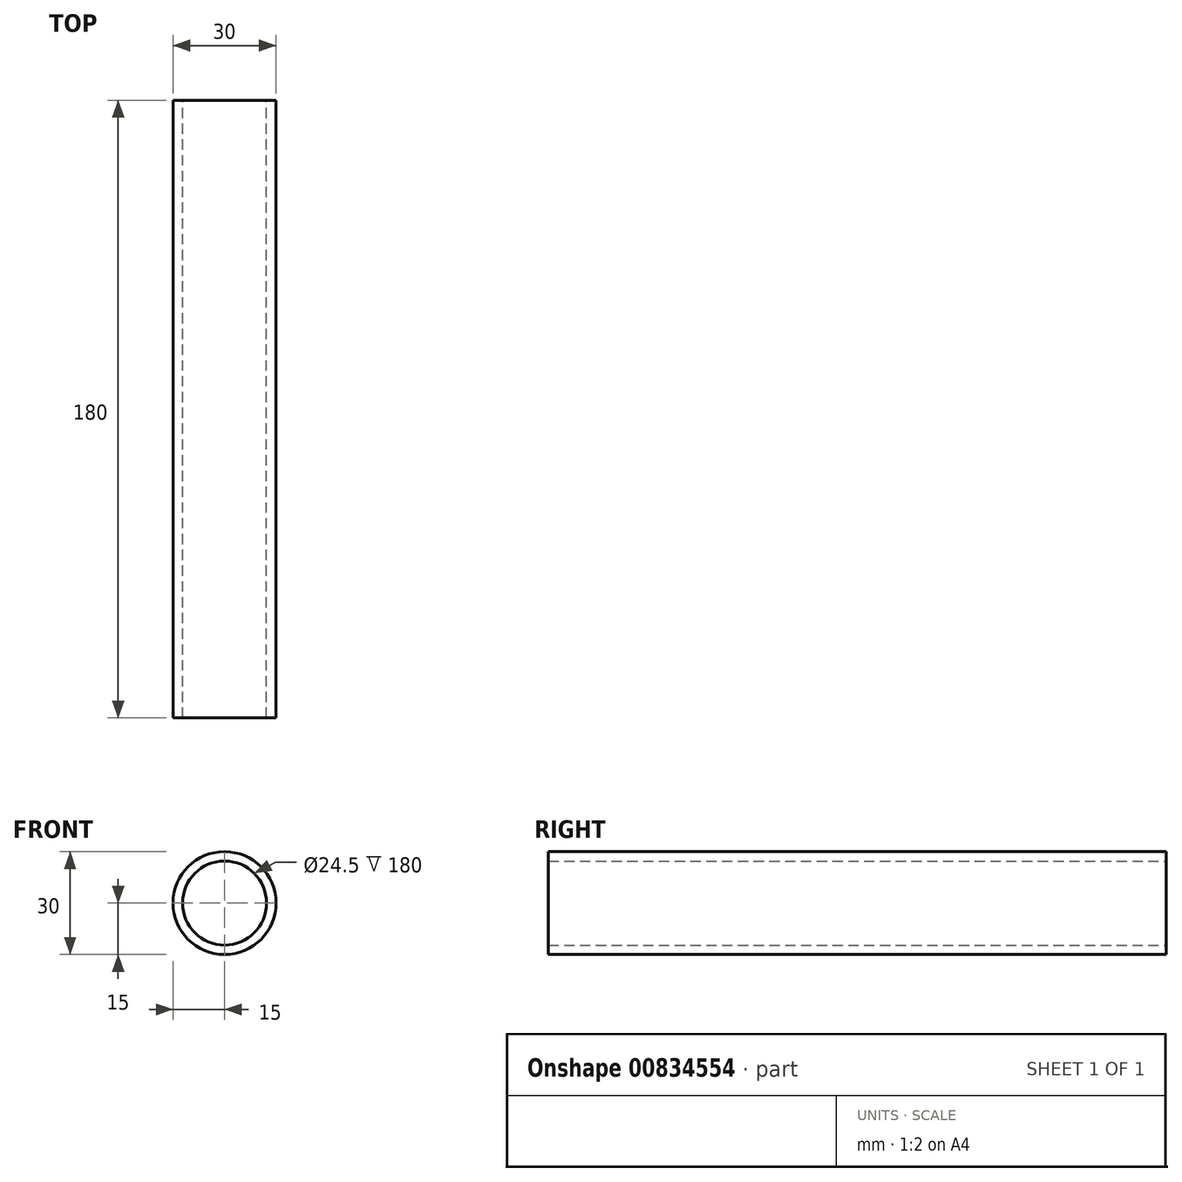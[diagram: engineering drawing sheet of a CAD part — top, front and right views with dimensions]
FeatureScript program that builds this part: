
annotation { "Feature Type Name" : "Feature", "Feature Type Description" : "" }
export const myFeature = defineFeature(function(context is Context, id is Id, definition is map)
    precondition{}
    {
        {
            var Q0;
            Q0=qCreatedBy(makeId("Front.planeOp"),FACE);
            var sketch = newSketch(context, id + "F0", { "sketchPlane" : qUnion([Q0])});
            skCircle(sketch, "E0", {"center": v(0, 0) * mm, "radius": 15 * mm});
            skSolve(sketch);
        }
        {
            var Q0;
            Q0 = qSketchRegion(id + "F0", true);
            extrude(context, id + "F1", {"entities" : qUnion([Q0]), "depth" : 180 * mm, "offsetDistance" : 25 * mm});
        }
        {
            var Q0;
            Q0=qCreatedBy(makeId("Front.planeOp"),FACE);
            var sketch = newSketch(context, id + "F2", { "sketchPlane" : qUnion([Q0])});
            skCircle(sketch, "E1", {"center": v(0, 0) * mm, "radius": 12.25 * mm});
            skSolve(sketch);
        }
        {
            var Q0;
            Q0 = qSketchRegion(id + "F2", true);
            extrude(context, id + "F3", {"entities" : qUnion([Q0]), "operationType" : NewBodyOperationType.REMOVE, "oppositeDirection" : true, "depth" : 180 * mm, "offsetDistance" : 25 * mm});
        }
        {
            var Q0;
            Q0=qCreatedBy(makeId("Front.planeOp"),FACE);
            var sketch = newSketch(context, id + "F4", { "sketchPlane" : qUnion([Q0])});
            skCircle(sketch, "E2", {"center": v(0, 0) * mm, "radius": 12.25 * mm});
            skSolve(sketch);
        }
        {
            var Q0;
            Q0 = qSketchRegion(id + "F4", true);
            extrude(context, id + "F5", {"entities" : qUnion([Q0]), "operationType" : NewBodyOperationType.REMOVE, "oppositeDirection" : true, "depth" : -180 * mm, "offsetDistance" : 25 * mm});
        }
        {
            var Q0;
            Q0=qCreatedBy(makeId("Front.planeOp"),FACE);
            var sketch = newSketch(context, id + "F6", { "sketchPlane" : qUnion([Q0])});
            skCircle(sketch, "E3", {"center": v(0, 0) * mm, "radius": 22.18 * mm});
            skSolve(sketch);
        }
        {
            var Q0;
            Q0=sQuery(id+"F6.wireOp",EDGE,"E3");
            extrude(context, id + "F7", {"bodyType" : ToolBodyType.SURFACE, "surfaceEntities" : qUnion([Q0]), "depth" : 76.7 * mm, "offsetDistance" : 25 * mm});
        }
    });
